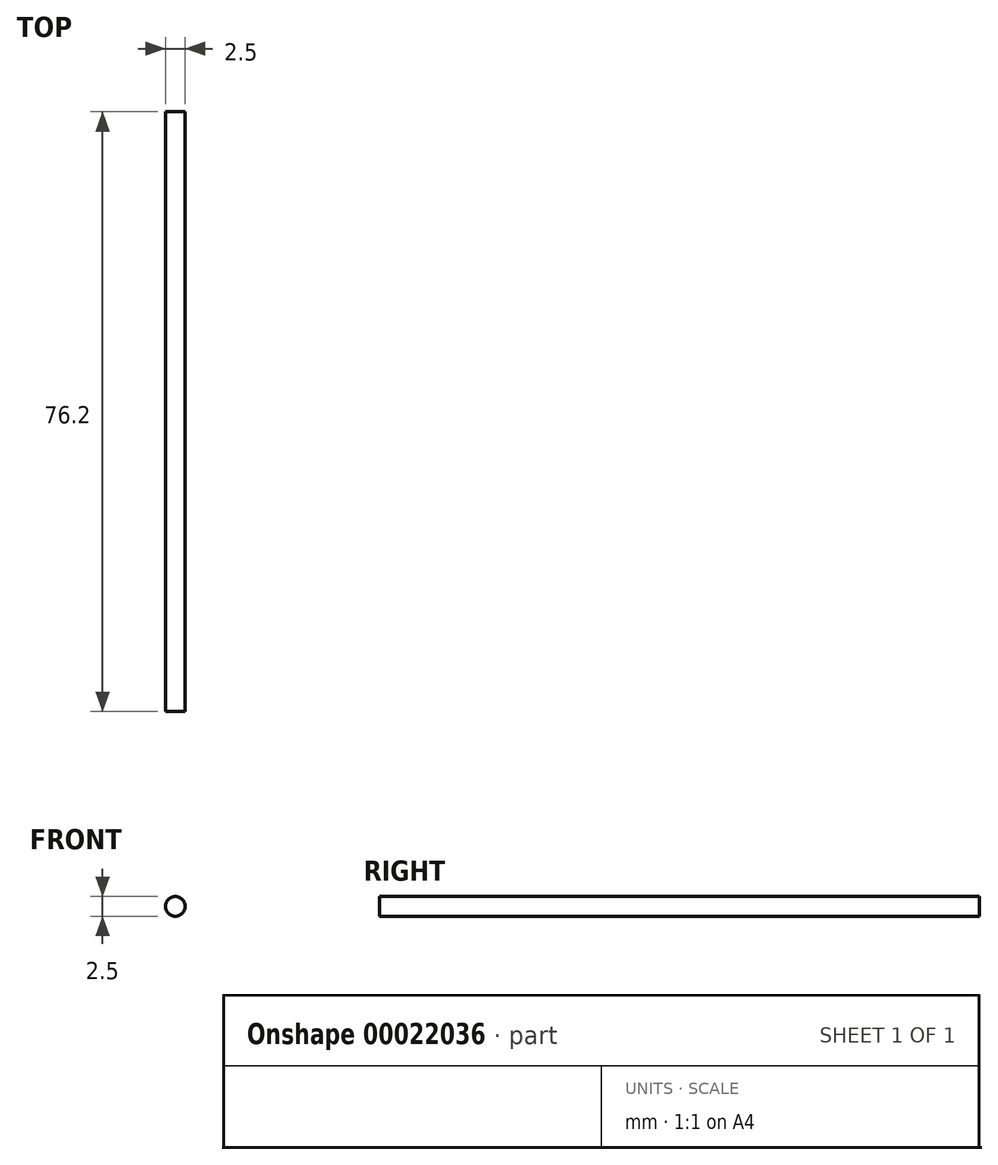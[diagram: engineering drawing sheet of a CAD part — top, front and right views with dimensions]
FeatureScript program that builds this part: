
annotation { "Feature Type Name" : "Feature", "Feature Type Description" : "" }
export const myFeature = defineFeature(function(context is Context, id is Id, definition is map)
    precondition{}
    {
        {
            var Q0;
            Q0=qCreatedBy(makeId("Front.planeOp"),FACE);
            var sketch = newSketch(context, id + "F0", { "sketchPlane" : qUnion([Q0])});
            skCircle(sketch, "E0", {"center": v(-63.47, 29.35) * mm, "radius": 1.25 * mm});
            skSolve(sketch);
        }
        {
            var Q0;
            Q0=makeQuery(id+"F0.imprint","IMPRINT",FACE,{"disambiguationData":[TD([[makeQuery(id+"F0.imprint","IMPRINT",EDGE,{"derivedFrom":sQuery(id+"F0.wireOp",EDGE,"E0")}),1.0]])]});
            extrude(context, id + "F1", {"entities" : qUnion([Q0]), "depth" : 76.2 * mm});
        }
    });
